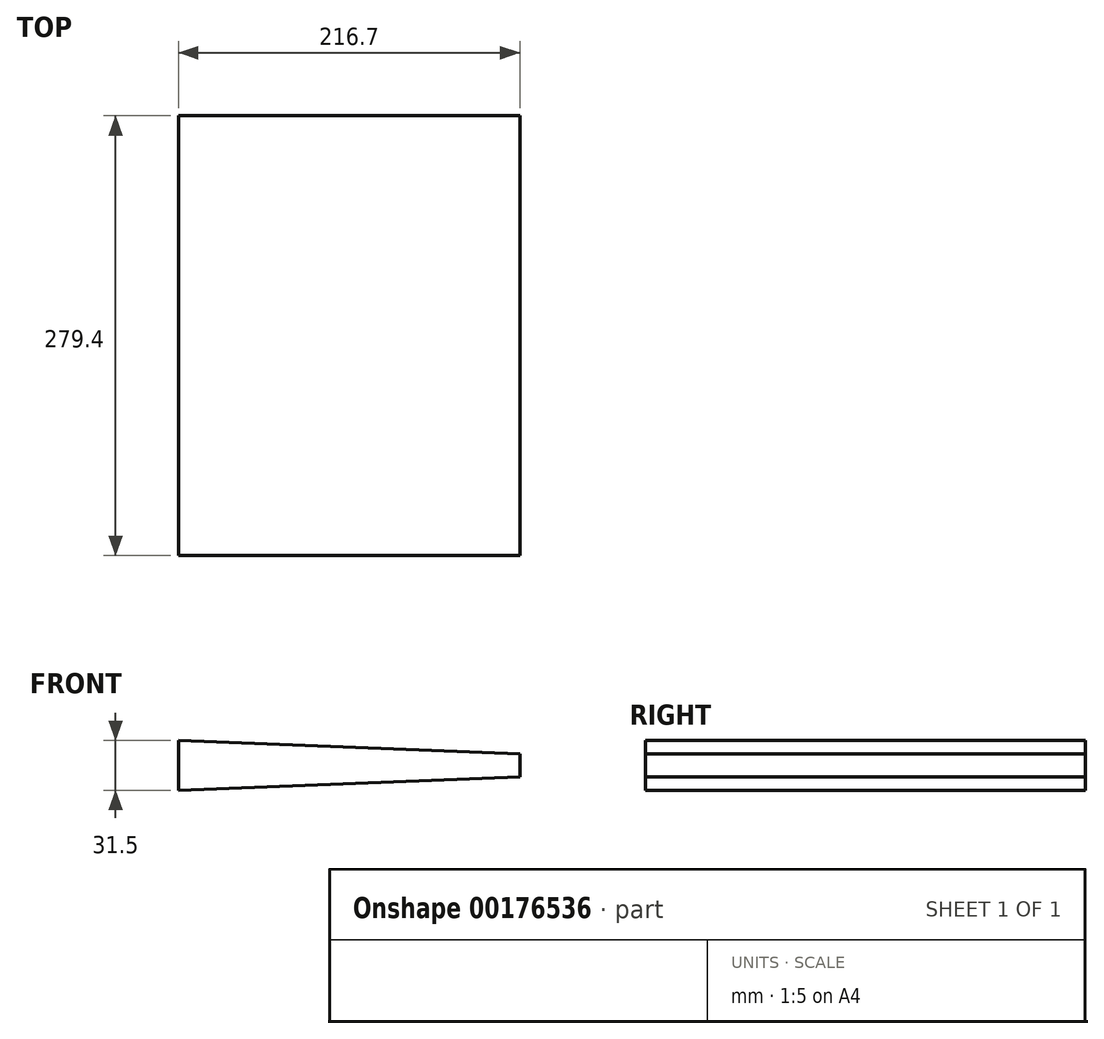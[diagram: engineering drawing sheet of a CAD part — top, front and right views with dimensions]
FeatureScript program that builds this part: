
annotation { "Feature Type Name" : "Feature", "Feature Type Description" : "" }
export const myFeature = defineFeature(function(context is Context, id is Id, definition is map)
    precondition{}
    {
        {
            var Q0;
            Q0=qCreatedBy(makeId("Front.planeOp"),FACE);
            var sketch = newSketch(context, id + "F0", { "sketchPlane" : qUnion([Q0])});
            skLineSegment(sketch, "E0.bottom", {"start": v(-114.3, 19.05) * mm, "end": v(114.3, 19.05) * mm, "construction": true});
            skLineSegment(sketch, "E0.top", {"start": v(-114.3, -19.05) * mm, "end": v(114.3, -19.05) * mm, "construction": true});
            skLineSegment(sketch, "E0.left", {"start": v(-114.3, 19.05) * mm, "end": v(-114.3, -19.05) * mm, "construction": true});
            skPoint(sketch, "E0.middle", {"position": v(0, 0) * mm});
            skLineSegment(sketch, "E1", {"start": v(114.3, -19.05) * mm, "end": v(114.3, 0) * mm, "construction": true});
            skLineSegment(sketch, "E2", {"start": v(114.3, 0) * mm, "end": v(114.3, 19.05) * mm, "construction": true});
            skLineSegment(sketch, "E3", {"start": v(-114.3, -19.05) * mm, "end": v(-114.3, 19.05) * mm});
            skLineSegment(sketch, "E4", {"start": v(114.3, 10.16) * mm, "end": v(-114.3, 19.05) * mm});
            skLineSegment(sketch, "E5", {"start": v(114.3, -10.16) * mm, "end": v(-114.3, -19.05) * mm});
            skLineSegment(sketch, "E6", {"start": v(114.3, 10.16) * mm, "end": v(114.3, 6.99) * mm});
            skLineSegment(sketch, "E7", {"start": v(114.3, -10.16) * mm, "end": v(114.3, -6.99) * mm});
            skLineSegment(sketch, "E8", {"start": v(114.3, 6.98) * mm, "end": v(-111.13, 15.75) * mm});
            skLineSegment(sketch, "E9", {"start": v(114.3, -6.99) * mm, "end": v(-111.13, -15.75) * mm});
            skLineSegment(sketch, "E10", {"start": v(-111.13, 15.75) * mm, "end": v(-111.13, -15.75) * mm});
            skLineSegment(sketch, "E11", {"start": v(105.58, 7.32) * mm, "end": v(105.58, -7.32) * mm});
            skSolve(sketch);
        }
        {
            var Q0;
            {var subQ0=sQuery(id+"F0.wireOp",EDGE,"E10");Q0=makeQuery(id+"F0.imprint","IMPRINT",FACE,{"disambiguationData":[TD([[makeQuery(id+"F0.imprint","IMPRINT",EDGE,{"derivedFrom":subQ0}),1.0]])]});}
            extrude(context, id + "F1", {"entities" : qUnion([Q0]), "depth" : 279.4 * mm});
        }
    });
